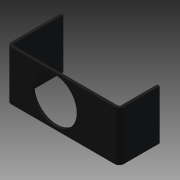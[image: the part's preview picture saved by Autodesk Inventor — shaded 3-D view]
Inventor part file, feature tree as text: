
AUTODESK INVENTOR PART (.ipt)
format: ipt  version: 2013 (Build 170138000, 138)  size: 111,616 bytes
history: native  units: in
note: dims shown in document units (in); Inventor stores cm internally (conversion verified against a paired STEP export)
features: extrude x2, sketch x2
ambient origin geometry x8: Origin, YZ Plane, XZ Plane, XY Plane, X Axis, Y Axis, Z Axis, Center Point
feature tree (4):
  extrude  "Extrusion3"  Depth=4.9213in
  extrude  "Extrusion4"  Depth=1.5748in
  sketch  "Sketch3"  dims[d8=0.1969in d9=4.9213in]
  sketch  "Sketch4"  dims[d11=0.1181in d12=1.5748in d13=2.1654in d14=0.0in d15=1.9685in d17=1.1024in d18=2.3622in d19=0.0in d21=2.0787in d22=2.1654in]
